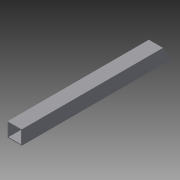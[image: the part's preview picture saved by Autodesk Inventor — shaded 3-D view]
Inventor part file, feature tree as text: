
AUTODESK INVENTOR PART (.ipt)
format: ipt  version: 2013 (Build 170138000, 138)  size: 87,552 bytes
history: native  units: in
note: dims shown in document units (in); Inventor stores cm internally (conversion verified against a paired STEP export)
features: extrude x2, sketch x2
ambient origin geometry x8: Origin, YZ Plane, XZ Plane, XY Plane, X Axis, Y Axis, Z Axis, Center Point
bodies: Solid1 (feature_tree)
feature tree (4):
  extrude  "Extrusion1"  TaperAngle=90.0deg  [1 undecoded]
  extrude  "Extrusion2"  TaperAngle=22.5deg  [1 undecoded]
  sketch  "Sketch1"  dims[d0=10.0in d1=90.0deg]
  sketch  "Sketch2"  dims[d2=22.5in d3=22.5deg d4=1.0in d5=180.0deg d6=1.0in d7=112.5deg d8=90.0deg d9=1.0in d10=0.0in d11=0.0625in d12=0.0625in d13=0.0625in d14=0.0625in d15=20.0in d16=0.0in]
note: 2 required parameter values undecoded (feature->parameter linkage not recoverable at this tier; creation-order binding heuristic only, values carry confidence <= 0.55)
